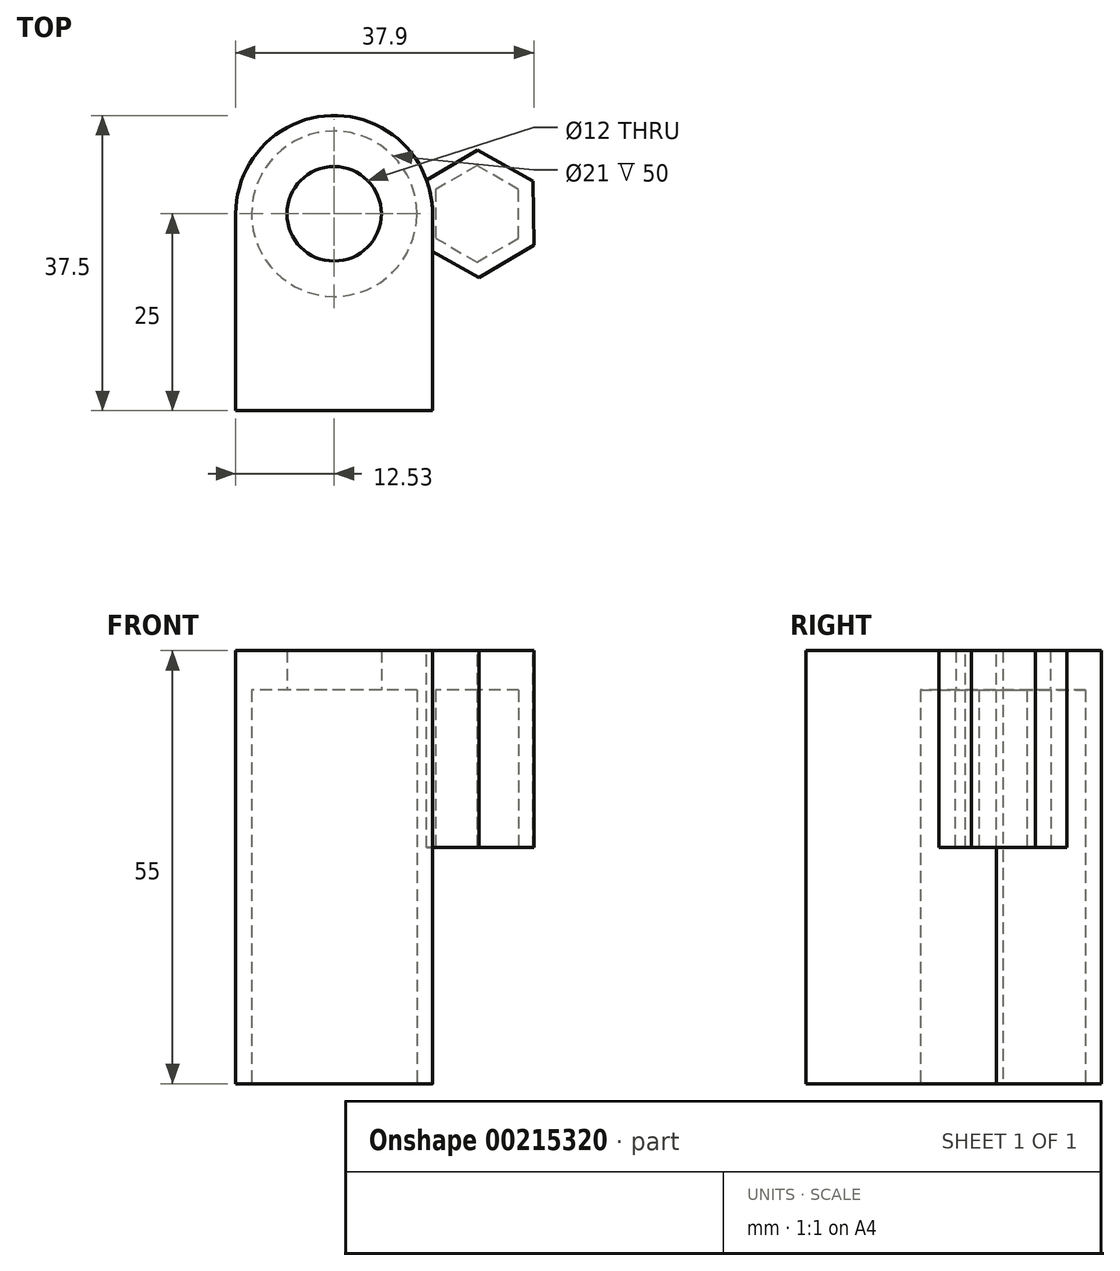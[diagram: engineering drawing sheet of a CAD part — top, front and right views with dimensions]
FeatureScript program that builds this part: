
annotation { "Feature Type Name" : "Feature", "Feature Type Description" : "" }
export const myFeature = defineFeature(function(context is Context, id is Id, definition is map)
    precondition{}
    {
        {
            var Q0;
            Q0=qCreatedBy(makeId("Top.planeOp"),FACE);
            var sketch = newSketch(context, id + "F7", { "sketchPlane" : qUnion([Q0])});
            skCircle(sketch, "E0", {"center": v(0, 0) * mm, "radius": 12.5 * mm});
            skSolve(sketch);
        }
        {
            var Q0;
            Q0=makeQuery(id+"F7.imprint","IMPRINT",FACE,{"disambiguationData":[TD([[makeQuery(id+"F7.imprint","IMPRINT",EDGE,{"derivedFrom":sQuery(id+"F7.wireOp",EDGE,"E0")}),1.0]])]});
            extrude(context, id + "F0", {"entities" : qUnion([Q0]), "depth" : 55 * mm});
        }
        {
            var Q0;
            Q0=qCreatedBy(makeId("Top.planeOp"),FACE);
            var sketch = newSketch(context, id + "F1", { "sketchPlane" : qUnion([Q0])});
            skLineSegment(sketch, "E1.bottom", {"start": v(-12.53, 0) * mm, "end": v(12.47, 0) * mm});
            skLineSegment(sketch, "E1.top", {"start": v(-12.53, -25) * mm, "end": v(12.47, -25) * mm});
            skLineSegment(sketch, "E1.left", {"start": v(-12.53, 0) * mm, "end": v(-12.53, -25) * mm});
            skLineSegment(sketch, "E1.right", {"start": v(12.47, 0) * mm, "end": v(12.47, -25) * mm});
            skSolve(sketch);
        }
        {
            var Q0;
            Q0=makeQuery(id+"F1.imprint","IMPRINT",FACE,{"disambiguationData":[TD([[makeQuery(id+"F1.imprint","IMPRINT",EDGE,{"derivedFrom":sQuery(id+"F1.wireOp",EDGE,"E1.bottom")}),-1.0]])]});
            extrude(context, id + "F8", {"entities" : qUnion([Q0]), "operationType" : NewBodyOperationType.ADD, "depth" : 55 * mm});
        }
        {
            var Q0;
            Q0=makeQuery(id+"F8.boolean.opBoolean","MERGE",FACE,{"derivedFrom":[makeQuery(id+"F0.opExtrude","CAP_FACE",FACE,{"disambiguationData":[OSD([sQuery(id+"F7.wireOp",EDGE,"E0")])],"isStart":true}),makeQuery(id+"F8.opExtrude","CAP_FACE",FACE,{"disambiguationData":[OSD([sQuery(id+"F1.wireOp",EDGE,"E1.bottom"),sQuery(id+"F1.wireOp",EDGE,"E1.top"),sQuery(id+"F1.wireOp",EDGE,"E1.left"),sQuery(id+"F1.wireOp",EDGE,"E1.right")])],"isStart":true})]});
            var sketch = newSketch(context, id + "F9", { "sketchPlane" : qUnion([Q0])});
            skPoint(sketch, "E2", {"position": v(0, 0) * mm});
            skSolve(sketch);
        }
        {
            var Q0;
            Q0=sQuery(id+"F9.wireOp",VERTEX,"E2");
            var Q1;
            Q1=makeQuery(id+"F0.opExtrude","SWEPT_BODY",BODY,{"disambiguationData":[OSD([sQuery(id+"F7.wireOp",EDGE,"E0")])]});
            hole(context, id + "F2", {"style" : HoleStyle.SIMPLE, "endStyle" : HoleEndStyle.THROUGH, "holeDiameter" : 12 * mm, "locations" : qUnion([Q0]), "scope" : qUnion([Q1]), "isTappedThrough" : true});
        }
        {
            var Q0;
            Q0=qCreatedBy(makeId("Top.planeOp"),FACE);
            var sketch = newSketch(context, id + "F10", { "sketchPlane" : qUnion([Q0])});
            skCircle(sketch, "E3", {"center": v(0, 0) * mm, "radius": 10.5 * mm});
            skSolve(sketch);
        }
        {
            var Q0;
            Q0=makeQuery(id+"F10.imprint","IMPRINT",FACE,{"disambiguationData":[TD([[makeQuery(id+"F10.imprint","IMPRINT",EDGE,{"derivedFrom":sQuery(id+"F10.wireOp",EDGE,"E3")}),1.0]])]});
            extrude(context, id + "F3", {"entities" : qUnion([Q0]), "operationType" : NewBodyOperationType.REMOVE, "depth" : 50 * mm});
        }
        {
            var Q0;
            Q0=makeQuery(id+"F8.boolean.opBoolean","MERGE",FACE,{"derivedFrom":[makeQuery(id+"F0.opExtrude","CAP_FACE",FACE,{"disambiguationData":[OSD([sQuery(id+"F7.wireOp",EDGE,"E0")])],"isStart":false}),makeQuery(id+"F8.opExtrude","CAP_FACE",FACE,{"disambiguationData":[OSD([sQuery(id+"F1.wireOp",EDGE,"E1.bottom"),sQuery(id+"F1.wireOp",EDGE,"E1.top"),sQuery(id+"F1.wireOp",EDGE,"E1.left"),sQuery(id+"F1.wireOp",EDGE,"E1.right")])],"isStart":false})]});
            var sketch = newSketch(context, id + "F4", { "sketchPlane" : qUnion([Q0])});
            skCircle(sketch, "E4.cCircle", {"center": v(18.3, 0) * mm, "radius": 8.1 * mm, "construction": true});
            skLineSegment(sketch, "E4.0", {"start": v(25.37, -3.97) * mm, "end": v(18.4, -8.1) * mm});
            skLineSegment(sketch, "E4.1", {"start": v(18.4, -8.1) * mm, "end": v(11.33, -4.13) * mm});
            skLineSegment(sketch, "E4.2", {"start": v(11.33, -4.13) * mm, "end": v(11.24, 3.97) * mm});
            skLineSegment(sketch, "E4.3", {"start": v(11.24, 3.97) * mm, "end": v(18.21, 8.1) * mm});
            skLineSegment(sketch, "E4.4", {"start": v(18.21, 8.1) * mm, "end": v(25.28, 4.13) * mm});
            skLineSegment(sketch, "E4.5", {"start": v(25.28, 4.13) * mm, "end": v(25.37, -3.97) * mm});
            skSolve(sketch);
        }
        {
            var Q0;
            {var subQ8=sQuery(id+"F4.wireOp",EDGE,"E4.0");Q0=makeQuery(id+"F4.imprint","IMPRINT",FACE,{"disambiguationData":[TD([[makeQuery(id+"F4.imprint","IMPRINT",EDGE,{"derivedFrom":subQ8}),-1.0]])]});}
            var sketch = newSketch(context, id + "F11", { "sketchPlane" : qUnion([Q0])});
            skSolve(sketch);
        }
        {
            var Q0;
            Q0 = qSketchRegion(id + "F11", true);
            var Q1;
            {var subQ7=sQuery(id+"F4.wireOp",EDGE,"E4.0");Q1=makeQuery(id+"F11.imprint","IMPRINT",FACE,{"disambiguationData":[TD([[makeQuery(id+"F11.imprint","IMPRINT",EDGE,{"derivedFrom":makeQuery(id+"F4.imprint","IMPRINT",EDGE,{"derivedFrom":subQ7})}),-1.0]])]});}
            extrude(context, id + "F5", {"entities" : qUnion([Q0, Q1]), "oppositeDirection" : true, "depth" : 25 * mm});
        }
        {
            var Q0;
            Q0=makeQuery(id+"F5.opExtrude","CAP_FACE",FACE,{"disambiguationData":[OSD([sQuery(id+"F7.wireOp",EDGE,"E0"),sQuery(id+"F1.wireOp",EDGE,"E1.right"),sQuery(id+"F4.wireOp",EDGE,"E4.0"),sQuery(id+"F4.wireOp",EDGE,"E4.1"),sQuery(id+"F4.wireOp",EDGE,"E4.3"),sQuery(id+"F4.wireOp",EDGE,"E4.4"),sQuery(id+"F4.wireOp",EDGE,"E4.5")])],"isStart":false});
            var sketch = newSketch(context, id + "F12", { "sketchPlane" : qUnion([Q0])});
            skCircle(sketch, "E5.cCircle", {"center": v(18.14, 0) * mm, "radius": 6.12 * mm, "construction": true});
            skPoint(sketch, "E5.cCircle.perimeterSnap0", {"position": v(21.75, -6.12) * mm});
            skLineSegment(sketch, "E5.0", {"start": v(18.14, -6.12) * mm, "end": v(12.84, -3.06) * mm});
            skPoint(sketch, "E5.0.startSnap0", {"position": v(21.75, -6.12) * mm});
            skLineSegment(sketch, "E5.1", {"start": v(12.84, -3.06) * mm, "end": v(12.84, 3.06) * mm});
            skLineSegment(sketch, "E5.2", {"start": v(12.84, 3.06) * mm, "end": v(18.14, 6.12) * mm});
            skLineSegment(sketch, "E5.3", {"start": v(18.14, 6.12) * mm, "end": v(23.44, 3.06) * mm});
            skLineSegment(sketch, "E5.4", {"start": v(23.44, 3.06) * mm, "end": v(23.44, -3.06) * mm});
            skLineSegment(sketch, "E5.5", {"start": v(23.44, -3.06) * mm, "end": v(18.14, -6.12) * mm});
            skSolve(sketch);
        }
        {
            var Q0;
            Q0=makeQuery(id+"F12.imprint","IMPRINT",FACE,{"disambiguationData":[TD([[makeQuery(id+"F12.imprint","IMPRINT",EDGE,{"derivedFrom":sQuery(id+"F12.wireOp",EDGE,"E5.0")}),-1.0]])]});
            extrude(context, id + "F6", {"entities" : qUnion([Q0]), "operationType" : NewBodyOperationType.REMOVE, "oppositeDirection" : true, "depth" : 20 * mm});
        }
    });
